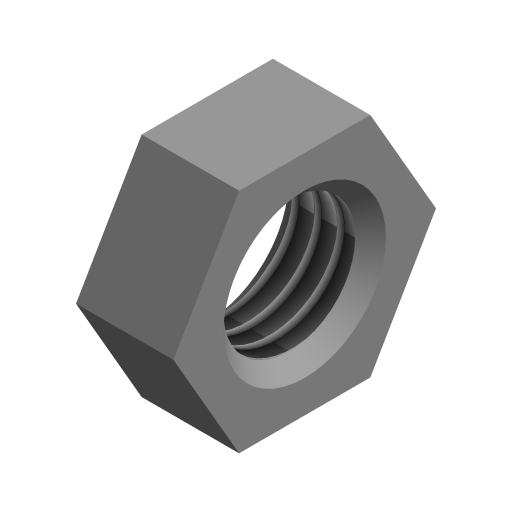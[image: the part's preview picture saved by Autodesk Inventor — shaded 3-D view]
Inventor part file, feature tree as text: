
AUTODESK INVENTOR PART (.ipt)
format: ipt  version: 2023.2 (Build 272271000, 271)  size: 132,608 bytes
history: native  units: mm (DEFAULTED — no unit token found)
features: other x14, sketch x3, revolve x2, thread x1, extrude x1
ambient origin geometry x8: Origin, YZ Plane, XZ Plane, XY Plane, X Axis, Y Axis, Z Axis, Center Point
bodies: Solid1 (feature_tree)
feature tree (21):
  revolve  "Revolution1"  Angle=360.0deg
  revolve  "Revolution2"  [1 undecoded]
  thread  "Thread1"  [1 undecoded]
  extrude  "Extrusion1"  Depth=3.0mm
  other  "cp_XY"
  other  "cp_YZ"
  other  "cp_ZX"
  other  "cp_X"
  other  "cp_Y"
  other  "cp_Z"
  other  "cp_Center"
  other  "nut_to_screw_XY"
  other  "nut_to_screw_YZ"
  other  "nut_to_screw_ZX"
  other  "nut_to_screw_X"
  other  "nut_to_screw_Y"
  other  "nut_to_screw_Z"
  other  "nut_to_screw_Center"
  sketch  "Sketch_5"  dims[d0=360.0deg d1=360.0deg]
  sketch  "Sketch_6"  dims[d2=1.642mm d3=0.0mm d4=3.0mm d5=0.0mm d6=0.0mm]
  sketch  "Sketch_7"  dims[d8=3.0mm d10=3.0mm]
note: 2 required parameter values undecoded (feature->parameter linkage not recoverable at this tier; creation-order binding heuristic only, values carry confidence <= 0.55)